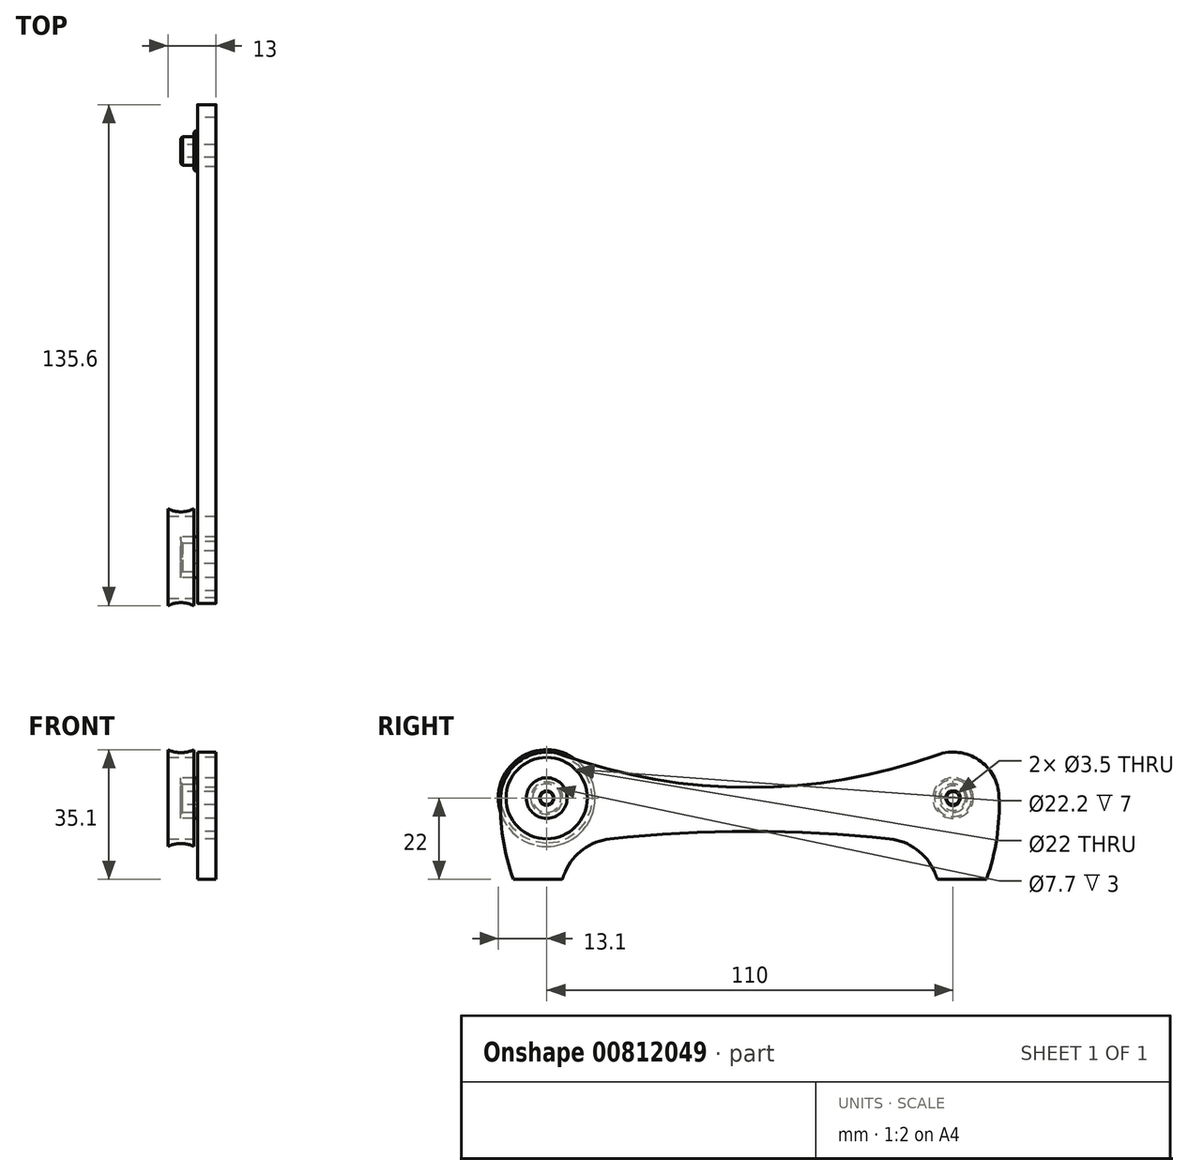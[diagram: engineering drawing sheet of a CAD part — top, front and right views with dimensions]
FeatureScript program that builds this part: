
annotation { "Feature Type Name" : "Feature", "Feature Type Description" : "" }
export const myFeature = defineFeature(function(context is Context, id is Id, definition is map)
    precondition{}
    {
        {
            var Q0;
            Q0=qCreatedBy(makeId("Right.planeOp"),FACE);
            var sketch = newSketch(context, id + "F0", { "sketchPlane" : qUnion([Q0])});
            skCircle(sketch, "E0", {"center": v(55, 22) * mm, "radius": 11 * mm});
            skCircle(sketch, "E1", {"center": v(0, 173.31) * mm, "radius": 150 * mm, "construction": true});
            skCircle(sketch, "E2.MirrorC", {"center": v(-55, 22) * mm, "radius": 11 * mm});
            skCircle(sketch, "E3", {"center": v(55, 22) * mm, "radius": 3.85 * mm});
            skCircle(sketch, "E4.MirrorC", {"center": v(-55, 22) * mm, "radius": 3.85 * mm});
            skArc(sketch, "E5", {"start": v(64.07, 0) * mm, "mid": v(66.84, 11.1) * mm, "end": v(67.45, 22.52) * mm});
            skArc(sketch, "E6", {"start": v(50.78, 0) * mm, "mid": v(48.27, 5.36) * mm, "end": v(44.75, 10.13) * mm});
            skArc(sketch, "E7.MirrorCS", {"start": v(-64.07, 0) * mm, "mid": v(-66.84, 11.1) * mm, "end": v(-67.45, 22.52) * mm});
            skArc(sketch, "E8.MirrorCS", {"start": v(-50.78, 0) * mm, "mid": v(-48.27, 5.36) * mm, "end": v(-44.75, 10.13) * mm});
            skLineSegment(sketch, "E9", {"start": v(50.78, 0) * mm, "end": v(64.07, 0) * mm});
            skLineSegment(sketch, "E10.MirrorCS", {"start": v(-50.78, 0) * mm, "end": v(-64.07, 0) * mm});
            skArc(sketch, "E11", {"start": v(44.75, 10.13) * mm, "mid": v(0, 13) * mm, "end": v(-44.75, 10.13) * mm});
            skArc(sketch, "E12", {"start": v(-50.78, 33.72) * mm, "mid": v(-61.95, 32.34) * mm, "end": v(-67.45, 22.52) * mm});
            skArc(sketch, "E13.MirrorC", {"start": v(50.78, 33.72) * mm, "mid": v(61.95, 32.34) * mm, "end": v(67.45, 22.52) * mm});
            skArc(sketch, "E14", {"start": v(-50.78, 33.72) * mm, "mid": v(0, 24.86) * mm, "end": v(50.78, 33.72) * mm});
            skCircle(sketch, "E15", {"center": v(55, 22) * mm, "radius": 5.5 * mm});
            skCircle(sketch, "E16.MirrorC", {"center": v(-55, 22) * mm, "radius": 5.5 * mm});
            skCircle(sketch, "E17", {"center": v(55, 22) * mm, "radius": 1.75 * mm});
            skCircle(sketch, "E18.MirrorC", {"center": v(-55, 22) * mm, "radius": 1.75 * mm});
            skSolve(sketch);
        }
        {
            var Q0;
            Q0=makeQuery(id+"F0.imprint","IMPRINT",FACE,{"disambiguationData":[TD([[makeQuery(id+"F0.imprint","IMPRINT",EDGE,{"derivedFrom":sQuery(id+"F0.wireOp",EDGE,"E0")}),-1.0]])]});
            var Q1;
            Q1=makeQuery(id+"F0.imprint","IMPRINT",FACE,{"disambiguationData":[TD([[makeQuery(id+"F0.imprint","IMPRINT",EDGE,{"derivedFrom":sQuery(id+"F0.wireOp",EDGE,"E0")}),1.0]])]});
            var Q2;
            Q2=makeQuery(id+"F0.imprint","IMPRINT",FACE,{"disambiguationData":[TD([[makeQuery(id+"F0.imprint","IMPRINT",EDGE,{"derivedFrom":sQuery(id+"F0.wireOp",EDGE,"E3")}),-1.0]])]});
            var Q3;
            Q3=makeQuery(id+"F0.imprint","IMPRINT",FACE,{"disambiguationData":[TD([[makeQuery(id+"F0.imprint","IMPRINT",EDGE,{"derivedFrom":sQuery(id+"F0.wireOp",EDGE,"E3")}),1.0]])]});
            var Q4;
            Q4=makeQuery(id+"F0.imprint","IMPRINT",FACE,{"disambiguationData":[TD([[makeQuery(id+"F0.imprint","IMPRINT",EDGE,{"derivedFrom":sQuery(id+"F0.wireOp",EDGE,"E2.MirrorC")}),-1.0]])]});
            var Q5;
            Q5=makeQuery(id+"F0.imprint","IMPRINT",FACE,{"disambiguationData":[TD([[makeQuery(id+"F0.imprint","IMPRINT",EDGE,{"derivedFrom":sQuery(id+"F0.wireOp",EDGE,"E4.MirrorC")}),1.0]])]});
            var Q6;
            Q6=makeQuery(id+"F0.imprint","IMPRINT",FACE,{"disambiguationData":[TD([[makeQuery(id+"F0.imprint","IMPRINT",EDGE,{"derivedFrom":sQuery(id+"F0.wireOp",EDGE,"E4.MirrorC")}),-1.0]])]});
            extrude(context, id + "F1", {"entities" : qUnion([Q0, Q1, Q2, Q3, Q4, Q5, Q6]), "depth" : 5 * mm, "offsetDistance" : 25 * mm});
        }
        {
            var Q0;
            Q0=makeQuery(id+"F0.imprint","IMPRINT",FACE,{"disambiguationData":[TD([[makeQuery(id+"F0.imprint","IMPRINT",EDGE,{"derivedFrom":sQuery(id+"F0.wireOp",EDGE,"E4.MirrorC")}),-1.0]])]});
            var Q1;
            Q1=makeQuery(id+"F0.imprint","IMPRINT",FACE,{"disambiguationData":[TD([[makeQuery(id+"F0.imprint","IMPRINT",EDGE,{"derivedFrom":sQuery(id+"F0.wireOp",EDGE,"E4.MirrorC")}),1.0]])]});
            var Q2;
            Q2=makeQuery(id+"F0.imprint","IMPRINT",FACE,{"disambiguationData":[TD([[makeQuery(id+"F0.imprint","IMPRINT",EDGE,{"derivedFrom":sQuery(id+"F0.wireOp",EDGE,"E3")}),1.0]])]});
            var Q3;
            Q3=makeQuery(id+"F0.imprint","IMPRINT",FACE,{"disambiguationData":[TD([[makeQuery(id+"F0.imprint","IMPRINT",EDGE,{"derivedFrom":sQuery(id+"F0.wireOp",EDGE,"E3")}),-1.0]])]});
            extrude(context, id + "F2", {"entities" : qUnion([Q0, Q1, Q2, Q3]), "operationType" : NewBodyOperationType.ADD, "oppositeDirection" : true, "depth" : 1 * mm, "offsetDistance" : 25 * mm});
        }
        {
            var Q0;
            Q0=makeQuery(id+"F0.imprint","IMPRINT",FACE,{"disambiguationData":[TD([[makeQuery(id+"F0.imprint","IMPRINT",EDGE,{"derivedFrom":sQuery(id+"F0.wireOp",EDGE,"E3")}),1.0]])]});
            var Q1;
            Q1=makeQuery(id+"F0.imprint","IMPRINT",FACE,{"disambiguationData":[TD([[makeQuery(id+"F0.imprint","IMPRINT",EDGE,{"derivedFrom":sQuery(id+"F0.wireOp",EDGE,"E4.MirrorC")}),-1.0]])]});
            extrude(context, id + "F3", {"entities" : qUnion([Q0, Q1]), "operationType" : NewBodyOperationType.ADD, "oppositeDirection" : true, "depth" : (7 / 2 + 1) * mm, "offsetDistance" : 25 * mm});
        }
        {
            var Q0;
            Q0=makeQuery(id+"F1.opExtrude","CAP_EDGE",EDGE,{"disambiguationData":[OSD([sQuery(id+"F0.wireOp",EDGE,"E17")])],"isStart":false});
            var Q1;
            Q1=makeQuery(id+"F1.opExtrude","CAP_EDGE",EDGE,{"disambiguationData":[OSD([sQuery(id+"F0.wireOp",EDGE,"E18.MirrorC")])],"isStart":false});
            chamfer(context, id + "F4", {"entities" : qUnion([Q0, Q1]), "width" : 0.2 * mm, "tangentPropagation" : true});
        }
        {
            var Q0;
            Q0=qCreatedBy(makeId("Front.planeOp"),FACE);
            var Q1;
            Q1=sQuery(id+"F0.wireOp",VERTEX,"E2.MirrorC.center");
            cPlane(context, id + "F5", {"entities" : qUnion([Q0, Q1]), "cplaneType" : CPlaneType.PLANE_POINT, "offset" : 25 * mm, "width" : 150 * mm, "height" : 150 * mm});
        }
        {
            var Q0;
            Q0=qCreatedBy(id+"F5.planeOp",FACE);
            var sketch = newSketch(context, id + "F6", { "sketchPlane" : qUnion([Q0])});
            skPoint(sketch, "E19.0", {"position": v(0, 22) * mm});
            skLineSegment(sketch, "E20", {"start": v(-1, 22) * mm, "end": v(-8, 22) * mm});
            skLineSegment(sketch, "E21", {"start": v(-8, 33.1) * mm, "end": v(-1, 33.1) * mm});
            skLineSegment(sketch, "E22", {"start": v(-1, 33.1) * mm, "end": v(-1, 35.1) * mm});
            skLineSegment(sketch, "E23", {"start": v(-4.5, 22) * mm, "end": v(-4.5, 24.58) * mm});
            skLineSegment(sketch, "E24.MirrorCS", {"start": v(-8, 33.1) * mm, "end": v(-8, 35.1) * mm});
            skPoint(sketch, "E25", {"position": v(-4.5, 33.1) * mm});
            skArc(sketch, "E26", {"start": v(-8, 35.1) * mm, "mid": v(-4.5, 34.3) * mm, "end": v(-1, 35.1) * mm});
            skSolve(sketch);
        }
        {
            var Q0;
            Q0=makeQuery(id+"F6.imprint","IMPRINT",FACE,{"disambiguationData":[TD([[makeQuery(id+"F6.imprint","IMPRINT",EDGE,{"derivedFrom":sQuery(id+"F6.wireOp",EDGE,"E21")}),1.0]])]});
            var Q1;
            Q1=sQuery(id+"F6.wireOp",EDGE,"E20");
            revolve(context, id + "F7", {"surfaceOperationType" : NewSurfaceOperationType.NEW, "entities" : qUnion([Q0]), "axis" : qUnion([Q1]), "revolveType" : RevolveType.FULL});
        }
        {
            var Q0;
            Q0=makeQuery(id+"F1.opExtrude","SWEPT_EDGE",EDGE,{"disambiguationData":[OSD([sQuery(id+"F0.wireOp",EDGE,"E8.MirrorCS"),sQuery(id+"F0.wireOp",EDGE,"E11")])]});
            var Q1;
            Q1=makeQuery(id+"F1.opExtrude","SWEPT_EDGE",EDGE,{"disambiguationData":[OSD([sQuery(id+"F0.wireOp",EDGE,"E6"),sQuery(id+"F0.wireOp",EDGE,"E11")])]});
            fillet(context, id + "F8", {"entities" : qUnion([Q0, Q1]), "radius" : 15 * mm, "tangentPropagation" : true, "allowEdgeOverflow" : false});
        }
        {
            var Q0;
            Q0=makeQuery(id+"F3.opExtrude","CAP_EDGE",EDGE,{"disambiguationData":[OSD([sQuery(id+"F0.wireOp",EDGE,"E4.MirrorC")])],"isStart":false});
            var Q1;
            Q1=makeQuery(id+"F3.opExtrude","CAP_EDGE",EDGE,{"disambiguationData":[OSD([sQuery(id+"F0.wireOp",EDGE,"E3")])],"isStart":false});
            var Q2;
            Q2=makeQuery(id+"F3.opExtrude","CAP_EDGE",EDGE,{"disambiguationData":[OSD([sQuery(id+"F0.wireOp",EDGE,"E17")])],"isStart":false});
            var Q3;
            Q3=makeQuery(id+"F2.opExtrude","CAP_EDGE",EDGE,{"disambiguationData":[OSD([sQuery(id+"F0.wireOp",EDGE,"E15")])],"isStart":false});
            var Q4;
            Q4=makeQuery(id+"F2.opExtrude","CAP_EDGE",EDGE,{"disambiguationData":[OSD([sQuery(id+"F0.wireOp",EDGE,"E16.MirrorC")])],"isStart":false});
            chamfer(context, id + "F9", {"entities" : qUnion([Q0, Q1, Q2, Q3, Q4]), "width" : 0.5 * mm, "tangentPropagation" : true});
        }
    });
